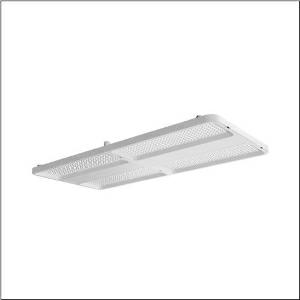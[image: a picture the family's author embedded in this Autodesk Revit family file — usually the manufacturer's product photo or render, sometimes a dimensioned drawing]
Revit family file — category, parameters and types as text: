
# Revit family: highbay_11_maxi_51hn12db4vda
name_source: partatom
category: Lighting Fixtures
units: mm (PartAtom-declared; Revit-internal decimal feet)

## family parameters
Cut with Voids When Loaded = No
Host = Face
Light Source = No
Part Type = Normal
Room Calculation Point = No
Round Connector Dimension = Use Diameter
Shared = No

## types (1)
- --- (1 x LED, 9070 lm, 44.6 W, 4000K)
    Apparent Load = 45 VA
    CIE Flux Codes = 87 98 100 100 100
    Color Rendering = 80
    Color Temperature = 4000K
    Default Elevation = 1800 mm
    Description = high bay luminaire Highbay 11 maxi; direct symmetric wide distribution, light control with lens of PMMA; UGR ≤ 22 (X = 4H | Y = 8H | S = 0.25H | reflection values 70/50/20); luminous flux: 56.000lm; light colour: 840, colour temperature: 4000K, MacAdam ≤ 2 SDCM (initial), colour rendering: CRI > 80; luminous efficacy: 189,9lm/W; rated service life: 100.000h (L95/B50) at AT= 25°C; control: DALI 2; housing frame of high-performance plastic PA6, matt traffic white (RAL 9016); cover of PMMA; dimension (LxWxH): 946 x 442 x 72mm; luminaire connection: terminal, 5-pole, max. 2.5mm² (cable entry for one cable, Ø 8.5..16mm); mains connection: 230..240V, AC/DC 0/50..60Hz; connected load: 294,9W; protection rating (complete): IP66; insulation class (complete): insulation class I (protective earthing); protection symbol: D; impact resistance: IK08; halogen-free wiring; for central battery installations according to DIN EN 60598-2-22; corresponds to IFS (International Featured Standards) requirements for safety and quality in the food industry; LABS conformity tested according to VDMA 24364:2018-05; certification: CE, ENEC, VDE, UKCA; permissible operating ambient temperature: -40..+50°C (reducing of maximum allowable ambient temperature of 5°C with ceiling mounting); packaging unit: 1 piece; (delivery without accessories; please order mounting accessories separately)
    Height = 72 mm  [stored 0.23622 ft]
    Lamp = 1 x LED
    Lamp Light Flux = 9070 lm
    Lamp Power = 44.6 W
    Lamp count = 1
    Length = 946 mm
    Luminous efficacy = 203 lm/W
    Manufacturer = Siteco
    ModVariant = No
    Model = 51HN12DB4VDA
    Mounting Place = Ceiling
    Mounting Type = Pendant
    Number of Poles = 1
    OnlyDefault = Yes
    Power Factor = 1
    Product Name = Highbay 11 maxi
    Product group = high bay luminaire
    ProductGroupID = 901
    Protection Class = Protection class I
    Protection Degree = IP 66
    RLX_Detail_Level = 1
    RLX_Emergency_Light_Flux = 0 lm
    RLX_Emergency_Type = 0
    RLX_Emergency_Type_DB = No
    RlxData = <blob elided: 22285 chars, md5=b82d0193>
    Socket = socket
    Standby Power = 0 W
    System Light Flux = 9070 lm
    System Power = 45 W
    Type Comments = : DC mode (central or group accumulator) initial emergency light level
    Type Image = l_1363244.jpg
    URL = http://relux.com
    VarID = @adj_005159
    Voltage = 0 V
    Weight = 0.00 kg
    Width = 442 mm

note: [stored X ft] marks values corroborated as IEEE doubles in the binary element streams (Revit-internal decimal feet)

## geometry (parser evidence)
native form markers: Blend x4, Sweep x12
no freeform markers — native parametric forms only
